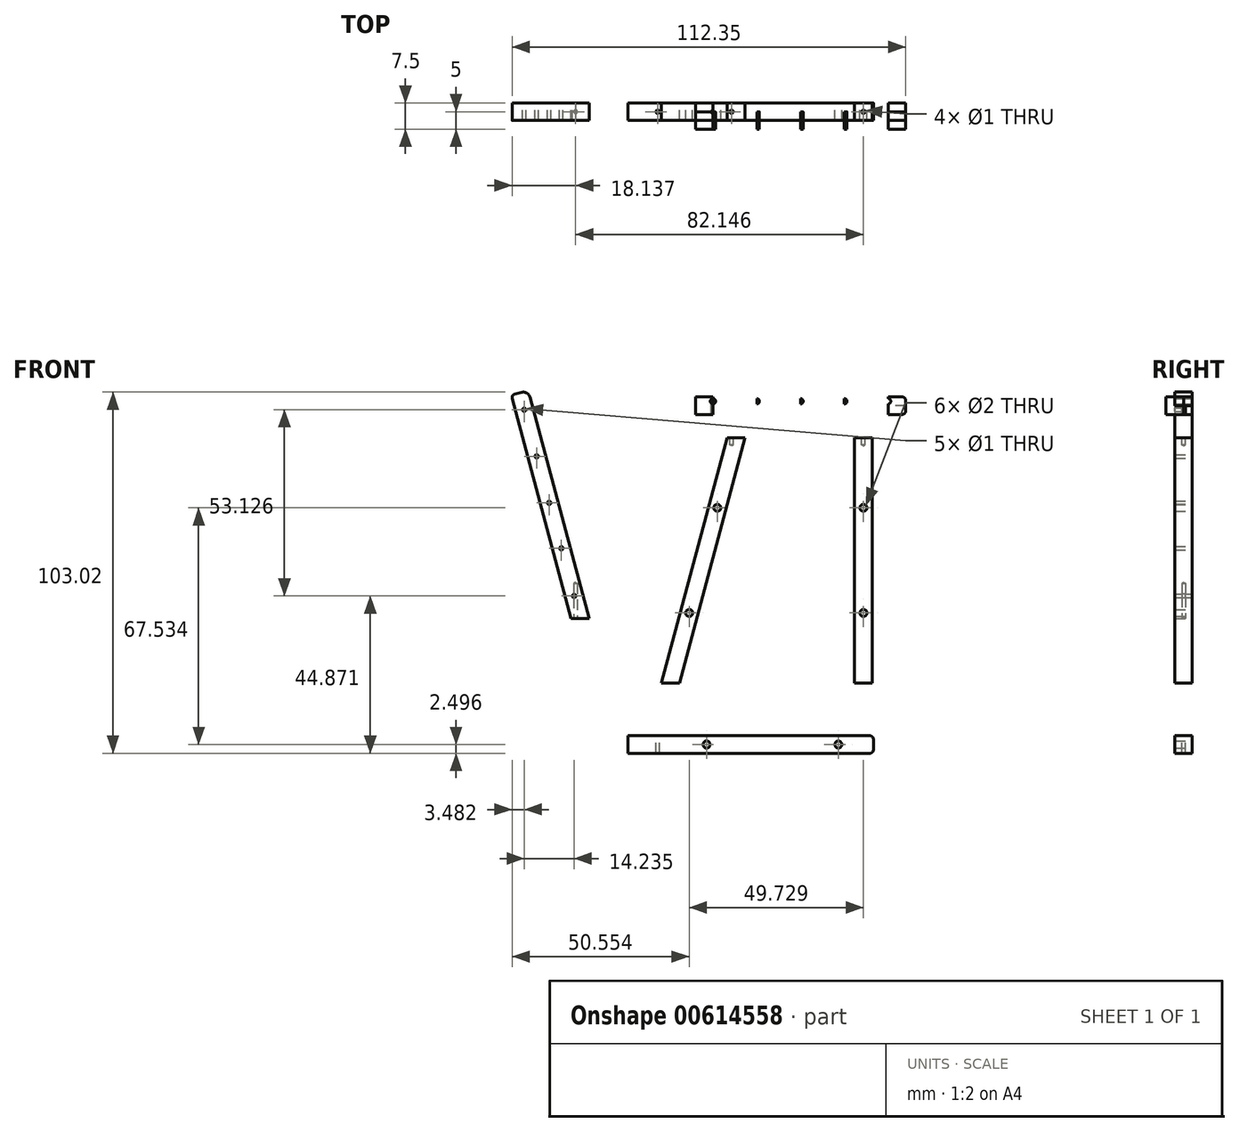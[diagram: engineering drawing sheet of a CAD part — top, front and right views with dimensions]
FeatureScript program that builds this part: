
annotation { "Feature Type Name" : "Feature", "Feature Type Description" : "" }
export const myFeature = defineFeature(function(context is Context, id is Id, definition is map)
    precondition{}
    {
        {
            var Q0;
            Q0=qCreatedBy(makeId("Front.planeOp"),FACE);
            var sketch = newSketch(context, id + "F0", { "sketchPlane" : qUnion([Q0])});
            skLineSegment(sketch, "E0.bottom", {"start": v(19.01, 34.3) * mm, "end": v(24.01, 34.3) * mm});
            skLineSegment(sketch, "E0.top", {"start": v(19.01, -35.7) * mm, "end": v(24.01, -35.7) * mm});
            skLineSegment(sketch, "E0.left", {"start": v(19.01, 34.3) * mm, "end": v(19.01, -35.7) * mm});
            skLineSegment(sketch, "E0.right", {"start": v(24.01, 34.3) * mm, "end": v(24.01, -35.7) * mm});
            skCircle(sketch, "E1", {"center": v(21.51, -15.7) * mm, "radius": 1 * mm});
            skCircle(sketch, "E2", {"center": v(21.51, 14.3) * mm, "radius": 1 * mm});
            skLineSegment(sketch, "E3.bottom", {"start": v(-17.4, 34.3) * mm, "end": v(-12.58, 33.02) * mm});
            skLineSegment(sketch, "E3.top", {"start": v(-35.82, -34.4) * mm, "end": v(-30.99, -35.7) * mm});
            skLineSegment(sketch, "E3.left", {"start": v(-17.4, 34.3) * mm, "end": v(-35.82, -34.4) * mm});
            skLineSegment(sketch, "E3.right", {"start": v(-12.58, 33.02) * mm, "end": v(-30.99, -35.7) * mm});
            skLineSegment(sketch, "E4", {"start": v(19.01, -35.7) * mm, "end": v(-30.99, -35.7) * mm});
            skLineSegment(sketch, "E5", {"start": v(-30.99, -35.7) * mm, "end": v(-36.16, -35.7) * mm});
            skLineSegment(sketch, "E6", {"start": v(-35.82, -34.4) * mm, "end": v(-36.16, -35.7) * mm});
            skLineSegment(sketch, "E7", {"start": v(-17.4, 34.3) * mm, "end": v(-12.23, 34.3) * mm});
            skLineSegment(sketch, "E8", {"start": v(-12.58, 33.02) * mm, "end": v(-12.23, 34.3) * mm});
            skCircle(sketch, "E9", {"center": v(-20.18, 14.3) * mm, "radius": 1 * mm});
            skCircle(sketch, "E10", {"center": v(-28.22, -15.7) * mm, "radius": 1 * mm});
            skLineSegment(sketch, "E11", {"start": v(21.51, 34.3) * mm, "end": v(21.51, 14.3) * mm});
            skLineSegment(sketch, "E12", {"start": v(21.51, -35.7) * mm, "end": v(21.51, -15.7) * mm});
            skLineSegment(sketch, "E13", {"start": v(-17.4, 34.3) * mm, "end": v(-14.82, 34.3) * mm});
            skLineSegment(sketch, "E14", {"start": v(-17.4, 34.3) * mm, "end": v(-16.11, 34.3) * mm});
            skSolve(sketch);
        }
        {
            var Q0;
            Q0=qCreatedBy(makeId("Front.planeOp"),FACE);
            var sketch = newSketch(context, id + "F1", { "sketchPlane" : qUnion([Q0])});
            skLineSegment(sketch, "E15.bottom", {"start": v(-26.42, 45.94) * mm, "end": v(32.58, 45.94) * mm});
            skLineSegment(sketch, "E15.top", {"start": v(-26.42, 40.94) * mm, "end": v(32.58, 40.94) * mm});
            skLineSegment(sketch, "E15.left", {"start": v(-26.42, 45.94) * mm, "end": v(-26.42, 40.94) * mm});
            skLineSegment(sketch, "E15.right", {"start": v(33.58, 44.94) * mm, "end": v(33.58, 41.94) * mm});
            skLineSegment(sketch, "E16", {"start": v(33.58, 43.44) * mm, "end": v(26.08, 43.44) * mm});
            skLineSegment(sketch, "E17", {"start": v(26.08, 43.44) * mm, "end": v(-15.61, 43.44) * mm});
            skCircle(sketch, "E18", {"center": v(-15.61, 43.44) * mm, "radius": 0.75 * mm});
            skCircle(sketch, "E19", {"center": v(26.08, 43.44) * mm, "radius": 0.75 * mm});
            skPoint(sketch, "E20.visualSharp", {"position": v(33.58, 45.94) * mm});
            skArc(sketch, "E20.filletArc", {"start": v(33.58, 44.94) * mm, "mid": v(33.29, 45.65) * mm, "end": v(32.58, 45.94) * mm});
            skPoint(sketch, "E21.visualSharp", {"position": v(33.58, 40.94) * mm});
            skArc(sketch, "E21.filletArc", {"start": v(32.58, 40.94) * mm, "mid": v(33.29, 41.23) * mm, "end": v(33.58, 41.94) * mm});
            skLineSegment(sketch, "E22", {"start": v(-26.42, 45.94) * mm, "end": v(-21.42, 45.94) * mm});
            skLineSegment(sketch, "E23", {"start": v(33.58, 45.94) * mm, "end": v(28.58, 45.94) * mm});
            skLineSegment(sketch, "E24", {"start": v(-21.42, 45.94) * mm, "end": v(-8.92, 45.94) * mm});
            skLineSegment(sketch, "E25", {"start": v(-8.92, 45.94) * mm, "end": v(3.58, 45.94) * mm});
            skLineSegment(sketch, "E26", {"start": v(3.58, 45.94) * mm, "end": v(16.08, 45.94) * mm});
            skLineSegment(sketch, "E27", {"start": v(16.08, 45.94) * mm, "end": v(28.58, 45.94) * mm});
            skLineSegment(sketch, "E28", {"start": v(-21.42, 45.94) * mm, "end": v(-21.42, 40.94) * mm});
            skLineSegment(sketch, "E29", {"start": v(-8.92, 45.94) * mm, "end": v(-8.92, 40.94) * mm});
            skLineSegment(sketch, "E30", {"start": v(3.58, 45.94) * mm, "end": v(3.58, 40.94) * mm});
            skLineSegment(sketch, "E31", {"start": v(16.08, 45.94) * mm, "end": v(16.08, 40.94) * mm});
            skLineSegment(sketch, "E32", {"start": v(28.58, 45.94) * mm, "end": v(28.58, 40.94) * mm});
            skLineSegment(sketch, "E33", {"start": v(-15.61, 43.44) * mm, "end": v(-21.42, 43.44) * mm});
            skLineSegment(sketch, "E34", {"start": v(-21.42, 43.44) * mm, "end": v(-21.42, 45.94) * mm});
            skLineSegment(sketch, "E35", {"start": v(-8.92, 45.94) * mm, "end": v(-8.92, 43.44) * mm});
            skLineSegment(sketch, "E36", {"start": v(-8.92, 45.94) * mm, "end": v(-8.92, 44.7) * mm});
            skLineSegment(sketch, "E37", {"start": v(3.58, 45.94) * mm, "end": v(3.58, 43.44) * mm});
            skLineSegment(sketch, "E38", {"start": v(3.58, 43.44) * mm, "end": v(3.58, 44.7) * mm});
            skLineSegment(sketch, "E39", {"start": v(16.08, 43.44) * mm, "end": v(16.08, 45.94) * mm});
            skLineSegment(sketch, "E40", {"start": v(28.58, 45.94) * mm, "end": v(28.58, 43.44) * mm});
            skLineSegment(sketch, "E41", {"start": v(28.58, 43.44) * mm, "end": v(28.58, 44.7) * mm});
            skLineSegment(sketch, "E42", {"start": v(-21.42, 45.94) * mm, "end": v(-21.42, 44.7) * mm});
            skCircle(sketch, "E43", {"center": v(-21.42, 44.7) * mm, "radius": 0.75 * mm});
            skCircle(sketch, "E44", {"center": v(-8.92, 44.7) * mm, "radius": 0.75 * mm});
            skCircle(sketch, "E45", {"center": v(3.58, 44.7) * mm, "radius": 0.75 * mm});
            skCircle(sketch, "E46", {"center": v(16.08, 44.7) * mm, "radius": 0.75 * mm});
            skCircle(sketch, "E47", {"center": v(28.58, 44.7) * mm, "radius": 0.75 * mm});
            skSolve(sketch);
        }
        {
            var Q0;
            {var subQ1=sQuery(id+"F1.wireOp",EDGE,"E15.bottom");Q0=makeQuery(id+"F1.imprint","IMPRINT",FACE,{"disambiguationData":[TD([[makeQuery(id+"F1.imprint","IMPRINT",EDGE,{"derivedFrom":subQ1}),-1.0]])]});}
            var Q1;
            {var subQ3=sQuery(id+"F0.wireOp",EDGE,"E0.left");Q1=makeQuery(id+"F0.imprint","IMPRINT",FACE,{"disambiguationData":[TD([[makeQuery(id+"F0.imprint","IMPRINT",EDGE,{"derivedFrom":subQ3}),1.0]])]});}
            var Q2;
            Q2=makeQuery(id+"F0.imprint","IMPRINT",FACE,{"disambiguationData":[TD([[makeQuery(id+"F0.imprint","IMPRINT",EDGE,{"derivedFrom":sQuery(id+"F0.wireOp",EDGE,"E3.bottom")}),-1.0]])]});
            var Q3;
            Q3=makeQuery(id+"F0.imprint","IMPRINT",FACE,{"disambiguationData":[TD([[makeQuery(id+"F0.imprint","IMPRINT",EDGE,{"derivedFrom":sQuery(id+"F0.wireOp",EDGE,"E3.bottom")}),1.0]])]});
            var Q4;
            Q4=makeQuery(id+"F0.imprint","IMPRINT",FACE,{"disambiguationData":[TD([[makeQuery(id+"F0.imprint","IMPRINT",EDGE,{"derivedFrom":sQuery(id+"F0.wireOp",EDGE,"E3.top")}),-1.0]])]});
            extrude(context, id + "F2", {"entities" : qUnion([Q0, Q1, Q2, Q3, Q4]), "endBound" : BoundingType.SYMMETRIC, "depth" : 5 * mm, "offsetDistance" : 25 * mm});
        }
        {
            var Q0;
            Q0=qCreatedBy(makeId("Front.planeOp"),FACE);
            var sketch = newSketch(context, id + "F3", { "sketchPlane" : qUnion([Q0])});
            skLineSegment(sketch, "E48.bottom", {"start": v(-45.64, -50.72) * mm, "end": v(23.36, -50.72) * mm});
            skLineSegment(sketch, "E48.top", {"start": v(-45.64, -55.72) * mm, "end": v(23.36, -55.72) * mm});
            skLineSegment(sketch, "E48.left", {"start": v(-45.64, -50.72) * mm, "end": v(-45.64, -55.72) * mm});
            skLineSegment(sketch, "E48.right", {"start": v(24.36, -51.72) * mm, "end": v(24.36, -54.72) * mm});
            skLineSegment(sketch, "E49", {"start": v(24.36, -53.22) * mm, "end": v(14.36, -53.22) * mm});
            skLineSegment(sketch, "E50", {"start": v(14.36, -53.22) * mm, "end": v(-23.26, -53.22) * mm});
            skCircle(sketch, "E51", {"center": v(-23.26, -53.22) * mm, "radius": 1 * mm});
            skCircle(sketch, "E52", {"center": v(14.36, -53.22) * mm, "radius": 1 * mm});
            skPoint(sketch, "E53.visualSharp", {"position": v(24.36, -50.72) * mm});
            skArc(sketch, "E53.filletArc", {"start": v(24.36, -51.72) * mm, "mid": v(24.07, -51.02) * mm, "end": v(23.36, -50.72) * mm});
            skPoint(sketch, "E54.visualSharp", {"position": v(24.36, -55.72) * mm});
            skArc(sketch, "E54.filletArc", {"start": v(23.36, -55.72) * mm, "mid": v(24.07, -55.43) * mm, "end": v(24.36, -54.72) * mm});
            skSolve(sketch);
        }
        {
            var Q0;
            Q0=makeQuery(id+"F3.imprint","IMPRINT",FACE,{"disambiguationData":[TD([[makeQuery(id+"F3.imprint","IMPRINT",EDGE,{"derivedFrom":sQuery(id+"F3.wireOp",EDGE,"E48.bottom")}),-1.0]])]});
            extrude(context, id + "F4", {"entities" : qUnion([Q0]), "endBound" : BoundingType.SYMMETRIC, "depth" : 5 * mm, "offsetDistance" : 25 * mm});
        }
        {
            var Q0;
            Q0=makeQuery(id+"F2.opExtrude","SWEPT_FACE",FACE,{"disambiguationData":[OSD([sQuery(id+"F0.wireOp",EDGE,"E7"),sQuery(id+"F0.wireOp",EDGE,"E13"),sQuery(id+"F0.wireOp",EDGE,"E14")])]});
            var sketch = newSketch(context, id + "F5", { "sketchPlane" : qUnion([Q0])});
            skLineSegment(sketch, "E55", {"start": v(-17.4, 0) * mm, "end": v(-12.23, 0) * mm});
            skLineSegment(sketch, "E56", {"start": v(-17.4, 0) * mm, "end": v(-14.82, 0) * mm});
            skLineSegment(sketch, "E57", {"start": v(-14.82, 0) * mm, "end": v(-16.11, 0) * mm});
            skSolve(sketch);
        }
        {
            var Q0;
            Q0=sQuery(id+"F5.wireOp",VERTEX,"E57.end");
            var Q1;
            Q1=makeQuery(id+"F2.opExtrude","SWEPT_BODY",BODY,{"disambiguationData":[OSD([sQuery(id+"F0.wireOp",EDGE,"E3.left"),sQuery(id+"F0.wireOp",EDGE,"E3.right"),sQuery(id+"F0.wireOp",EDGE,"E5"),sQuery(id+"F0.wireOp",EDGE,"E6"),sQuery(id+"F0.wireOp",EDGE,"E7"),sQuery(id+"F0.wireOp",EDGE,"E8"),sQuery(id+"F0.wireOp",EDGE,"E9"),sQuery(id+"F0.wireOp",EDGE,"E10"),sQuery(id+"F0.wireOp",EDGE,"E13"),sQuery(id+"F0.wireOp",EDGE,"E14")])]});
            hole(context, id + "F6", {"style" : HoleStyle.SIMPLE, "endStyle" : HoleEndStyle.BLIND, "holeDiameter" : 1 * mm, "majorDiameter" : 5 * mm, "holeDepth" : 2 * mm, "isTappedThrough" : true, "tappedDepth" : 12 * mm, "tapClearance" : 3, "locations" : qUnion([Q0]), "scope" : qUnion([Q1])});
        }
        {
            var Q0;
            Q0=makeQuery(id+"F2.opExtrude","SWEPT_FACE",FACE,{"disambiguationData":[OSD([sQuery(id+"F0.wireOp",EDGE,"E0.bottom")])]});
            var sketch = newSketch(context, id + "F7", { "sketchPlane" : qUnion([Q0])});
            skLineSegment(sketch, "E58", {"start": v(19.01, 0) * mm, "end": v(24.01, 0) * mm});
            skLineSegment(sketch, "E59", {"start": v(19.01, 0) * mm, "end": v(21.51, 0) * mm});
            skSolve(sketch);
        }
        {
            var Q0;
            Q0=sQuery(id+"F7.wireOp",VERTEX,"E59.end");
            var Q1;
            Q1=makeQuery(id+"F2.opExtrude","SWEPT_BODY",BODY,{"disambiguationData":[OSD([sQuery(id+"F0.wireOp",EDGE,"E0.bottom"),sQuery(id+"F0.wireOp",EDGE,"E0.top"),sQuery(id+"F0.wireOp",EDGE,"E0.left"),sQuery(id+"F0.wireOp",EDGE,"E0.right"),sQuery(id+"F0.wireOp",EDGE,"E1"),sQuery(id+"F0.wireOp",EDGE,"E2")])]});
            hole(context, id + "F8", {"style" : HoleStyle.SIMPLE, "endStyle" : HoleEndStyle.BLIND, "holeDiameter" : 1 * mm, "majorDiameter" : 5 * mm, "holeDepth" : 2 * mm, "isTappedThrough" : true, "tappedDepth" : 12 * mm, "tapClearance" : 3, "locations" : qUnion([Q0]), "scope" : qUnion([Q1])});
        }
        {
            var Q0;
            Q0=qCreatedBy(makeId("Front.planeOp"),FACE);
            var sketch = newSketch(context, id + "F9", { "sketchPlane" : qUnion([Q0])});
            skLineSegment(sketch, "E60.bottom", {"start": v(-79, 46.46) * mm, "end": v(-74.17, 47.75) * mm});
            skLineSegment(sketch, "E60.top", {"start": v(-61.93, -17.25) * mm, "end": v(-57.1, -15.95) * mm});
            skLineSegment(sketch, "E60.left", {"start": v(-79, 46.46) * mm, "end": v(-61.93, -17.25) * mm});
            skLineSegment(sketch, "E60.right", {"start": v(-74.17, 47.75) * mm, "end": v(-57.1, -15.95) * mm});
            skLineSegment(sketch, "E61", {"start": v(-61.93, -17.25) * mm, "end": v(-56.75, -17.25) * mm});
            skLineSegment(sketch, "E62", {"start": v(-57.1, -15.95) * mm, "end": v(-56.75, -17.25) * mm});
            skLineSegment(sketch, "E63", {"start": v(-59.34, -17.25) * mm, "end": v(-64.7, 2.75) * mm});
            skCircle(sketch, "E64", {"center": v(-64.7, 2.75) * mm, "radius": 0.5 * mm});
            skLineSegment(sketch, "E65", {"start": v(-64.7, 2.75) * mm, "end": v(-76.58, 47.1) * mm});
            skLineSegment(sketch, "E66", {"start": v(-76.58, 47.1) * mm, "end": v(-75.29, 42.28) * mm});
            skLineSegment(sketch, "E67", {"start": v(-75.29, 42.28) * mm, "end": v(-71.73, 29) * mm});
            skLineSegment(sketch, "E68", {"start": v(-71.73, 29) * mm, "end": v(-68.17, 15.71) * mm});
            skLineSegment(sketch, "E69", {"start": v(-68.17, 15.71) * mm, "end": v(-64.61, 2.43) * mm});
            skLineSegment(sketch, "E70", {"start": v(-64.61, 2.43) * mm, "end": v(-61.05, -10.85) * mm});
            skCircle(sketch, "E71", {"center": v(-61.05, -10.85) * mm, "radius": 0.5 * mm});
            skCircle(sketch, "E72", {"center": v(-75.29, 42.28) * mm, "radius": 0.5 * mm});
            skCircle(sketch, "E73", {"center": v(-71.73, 29) * mm, "radius": 0.5 * mm});
            skCircle(sketch, "E74", {"center": v(-68.17, 15.71) * mm, "radius": 0.5 * mm});
            skSolve(sketch);
        }
        {
            var Q0;
            Q0=makeQuery(id+"F2.opExtrude","SWEPT_FACE",FACE,{"disambiguationData":[OSD([sQuery(id+"F1.wireOp",EDGE,"E15.bottom")])]});
            var sketch = newSketch(context, id + "F10", { "sketchPlane" : qUnion([Q0])});
            skLineSegment(sketch, "E75", {"start": v(-26.42, 0) * mm, "end": v(-21.42, 0) * mm});
            skPoint(sketch, "E75.endSnap0", {"position": v(-26.42, 0) * mm});
            skSolve(sketch);
        }
        {
            var Q0;
            Q0=makeQuery(id+"F9.imprint","IMPRINT",FACE,{"disambiguationData":[TD([[makeQuery(id+"F9.imprint","IMPRINT",EDGE,{"derivedFrom":sQuery(id+"F9.wireOp",EDGE,"E60.bottom")}),-1.0]])]});
            var Q1;
            {var subQ0=sQuery(id+"F9.wireOp",EDGE,"E62");Q1=makeQuery(id+"F9.imprint","IMPRINT",FACE,{"disambiguationData":[TD([[makeQuery(id+"F9.imprint","IMPRINT",EDGE,{"derivedFrom":subQ0}),-1.0]])]});}
            var Q2;
            {var subQ0=sQuery(id+"F9.wireOp",EDGE,"E61");var subQ3=sQuery(id+"F9.wireOp",EDGE,"E63");var subQ5=makeQuery(id+"F9.imprint","INTERSECT",VERTEX,{"derivedFrom":[subQ0,subQ3]});Q2=makeQuery(id+"F9.imprint","IMPRINT",FACE,{"disambiguationData":[TD([[makeQuery(id+"F9.imprint","IMPRINT",EDGE,{"disambiguationData":[TD([[subQ5,-1.0]])],"derivedFrom":subQ3}),1.0]])]});}
            extrude(context, id + "F11", {"entities" : qUnion([Q0, Q1, Q2]), "endBound" : BoundingType.SYMMETRIC, "depth" : 5 * mm, "offsetDistance" : 25 * mm});
        }
        {
            var Q0;
            Q0=makeQuery(id+"F11.opExtrude","SWEPT_FACE",FACE,{"disambiguationData":[OSD([sQuery(id+"F9.wireOp",EDGE,"E61")])]});
            var sketch = newSketch(context, id + "F12", { "sketchPlane" : qUnion([Q0])});
            skLineSegment(sketch, "E76", {"start": v(-61.93, 0) * mm, "end": v(-56.75, 0) * mm});
            skLineSegment(sketch, "E77", {"start": v(-56.75, 0) * mm, "end": v(-59.34, 0) * mm});
            skLineSegment(sketch, "E78", {"start": v(-59.34, 0) * mm, "end": v(-61.93, 0) * mm});
            skLineSegment(sketch, "E79", {"start": v(-61.93, 0) * mm, "end": v(-60.63, 0) * mm});
            skSolve(sketch);
        }
        {
            var Q0;
            Q0=sQuery(id+"F12.wireOp",VERTEX,"E79.end");
            var Q1;
            Q1=makeQuery(id+"F11.opExtrude","SWEPT_BODY",BODY,{"disambiguationData":[OSD([sQuery(id+"F9.wireOp",EDGE,"E60.bottom"),sQuery(id+"F9.wireOp",EDGE,"E60.left"),sQuery(id+"F9.wireOp",EDGE,"E60.right"),sQuery(id+"F9.wireOp",EDGE,"E61"),sQuery(id+"F9.wireOp",EDGE,"E62"),sQuery(id+"F9.wireOp",EDGE,"E64")])]});
            hole(context, id + "F13", {"style" : HoleStyle.SIMPLE, "endStyle" : HoleEndStyle.BLIND, "holeDiameter" : 1 * mm, "majorDiameter" : 5 * mm, "holeDepth" : 10 * mm, "isTappedThrough" : true, "tappedDepth" : 12 * mm, "tapClearance" : 3, "locations" : qUnion([Q0]), "scope" : qUnion([Q1])});
        }
        {
            var Q0;
            Q0=sQuery(id+"F10.wireOp",VERTEX,"E75.end");
            var Q1;
            Q1=makeQuery(id+"F2.opExtrude","SWEPT_BODY",BODY,{"disambiguationData":[OSD([sQuery(id+"F1.wireOp",EDGE,"E15.bottom"),sQuery(id+"F1.wireOp",EDGE,"E15.top"),sQuery(id+"F1.wireOp",EDGE,"E15.left"),sQuery(id+"F1.wireOp",EDGE,"E15.right"),sQuery(id+"F1.wireOp",EDGE,"E18"),sQuery(id+"F1.wireOp",EDGE,"E19"),sQuery(id+"F1.wireOp",EDGE,"E20.filletArc"),sQuery(id+"F1.wireOp",EDGE,"E21.filletArc")])]});
            hole(context, id + "F14", {"style" : HoleStyle.SIMPLE, "endStyle" : HoleEndStyle.BLIND, "holeDiameter" : 1 * mm, "majorDiameter" : 5 * mm, "holeDepth" : 10 * mm, "isTappedThrough" : true, "tappedDepth" : 12 * mm, "tapClearance" : 3, "locations" : qUnion([Q0]), "scope" : qUnion([Q1])});
        }
        {
            var Q0;
            Q0=makeQuery(id+"F4.opExtrude","SWEPT_FACE",FACE,{"disambiguationData":[OSD([sQuery(id+"F3.wireOp",EDGE,"E48.bottom")])]});
            var sketch = newSketch(context, id + "F15", { "sketchPlane" : qUnion([Q0])});
            skPoint(sketch, "E80.endSnap0", {"position": v(-45.64, 0) * mm});
            skLineSegment(sketch, "E81", {"start": v(-45.64, 0) * mm, "end": v(-37.2, 0) * mm});
            skSolve(sketch);
        }
        {
            var Q0;
            Q0=sQuery(id+"F15.wireOp",VERTEX,"E81.end");
            var Q1;
            Q1=makeQuery(id+"F4.opExtrude","SWEPT_BODY",BODY,{"disambiguationData":[OSD([sQuery(id+"F3.wireOp",EDGE,"E48.bottom"),sQuery(id+"F3.wireOp",EDGE,"E48.top"),sQuery(id+"F3.wireOp",EDGE,"E48.left"),sQuery(id+"F3.wireOp",EDGE,"E48.right"),sQuery(id+"F3.wireOp",EDGE,"E51"),sQuery(id+"F3.wireOp",EDGE,"E52"),sQuery(id+"F3.wireOp",EDGE,"E53.filletArc"),sQuery(id+"F3.wireOp",EDGE,"E54.filletArc")])]});
            hole(context, id + "F16", {"style" : HoleStyle.SIMPLE, "endStyle" : HoleEndStyle.BLIND, "holeDiameter" : 1 * mm, "majorDiameter" : 5 * mm, "holeDepth" : 10 * mm, "isTappedThrough" : true, "tappedDepth" : 12 * mm, "tapClearance" : 3, "locations" : qUnion([Q0]), "scope" : qUnion([Q1])});
        }
        {
            var Q0;
            Q0=makeQuery(id+"F11.opExtrude","SWEPT_EDGE",EDGE,{"disambiguationData":[OSD([sQuery(id+"F9.wireOp",EDGE,"E60.bottom"),sQuery(id+"F9.wireOp",EDGE,"E60.left")])]});
            fillet(context, id + "F17", {"entities" : qUnion([Q0]), "radius" : 1 * mm, "tangentPropagation" : true, "allowEdgeOverflow" : false});
        }
        {
            var Q0;
            Q0=makeQuery(id+"F11.opExtrude","SWEPT_EDGE",EDGE,{"disambiguationData":[OSD([sQuery(id+"F9.wireOp",EDGE,"E60.bottom"),sQuery(id+"F9.wireOp",EDGE,"E60.right")])]});
            fillet(context, id + "F18", {"entities" : qUnion([Q0]), "radius" : 2 * mm, "tangentPropagation" : true, "allowEdgeOverflow" : false});
        }
        {
            var Q0;
            {var subQ1=sQuery(id+"F1.wireOp",EDGE,"E15.left");Q0=makeQuery(id+"F1.imprint","IMPRINT",FACE,{"disambiguationData":[TD([[makeQuery(id+"F1.imprint","IMPRINT",EDGE,{"derivedFrom":subQ1}),1.0]])]});}
            var Q1;
            {var subQ0=sQuery(id+"F1.wireOp",EDGE,"E28");Q1=makeQuery(id+"F1.imprint","IMPRINT",FACE,{"disambiguationData":[TD([[makeQuery(id+"F1.imprint","IMPRINT",EDGE,{"derivedFrom":subQ0}),1.0]])]});}
            var Q2;
            {var subQ13=sQuery(id+"F1.wireOp",EDGE,"E24");Q2=makeQuery(id+"F1.imprint","IMPRINT",FACE,{"disambiguationData":[TD([[makeQuery(id+"F1.imprint","IMPRINT",EDGE,{"derivedFrom":subQ13}),-1.0]])]});}
            var Q3;
            {var subQ0=sQuery(id+"F1.wireOp",EDGE,"E29");Q3=makeQuery(id+"F1.imprint","IMPRINT",FACE,{"disambiguationData":[TD([[makeQuery(id+"F1.imprint","IMPRINT",EDGE,{"derivedFrom":subQ0}),1.0]])]});}
            var Q4;
            {var subQ1=sQuery(id+"F1.wireOp",EDGE,"E25");Q4=makeQuery(id+"F1.imprint","IMPRINT",FACE,{"disambiguationData":[TD([[makeQuery(id+"F1.imprint","IMPRINT",EDGE,{"derivedFrom":subQ1}),-1.0]])]});}
            var Q5;
            {var subQ0=sQuery(id+"F1.wireOp",EDGE,"E30");Q5=makeQuery(id+"F1.imprint","IMPRINT",FACE,{"disambiguationData":[TD([[makeQuery(id+"F1.imprint","IMPRINT",EDGE,{"derivedFrom":subQ0}),1.0]])]});}
            var Q6;
            {var subQ6=sQuery(id+"F1.wireOp",EDGE,"E26");Q6=makeQuery(id+"F1.imprint","IMPRINT",FACE,{"disambiguationData":[TD([[makeQuery(id+"F1.imprint","IMPRINT",EDGE,{"derivedFrom":subQ6}),-1.0]])]});}
            var Q7;
            {var subQ6=sQuery(id+"F1.wireOp",EDGE,"E31");Q7=makeQuery(id+"F1.imprint","IMPRINT",FACE,{"disambiguationData":[TD([[makeQuery(id+"F1.imprint","IMPRINT",EDGE,{"derivedFrom":subQ6}),1.0]])]});}
            var Q8;
            {var subQ0=sQuery(id+"F1.wireOp",EDGE,"E27");Q8=makeQuery(id+"F1.imprint","IMPRINT",FACE,{"disambiguationData":[TD([[makeQuery(id+"F1.imprint","IMPRINT",EDGE,{"derivedFrom":subQ0}),-1.0]])]});}
            var Q9;
            {var subQ1=sQuery(id+"F1.wireOp",EDGE,"E20.filletArc");Q9=makeQuery(id+"F1.imprint","IMPRINT",FACE,{"disambiguationData":[TD([[makeQuery(id+"F1.imprint","IMPRINT",EDGE,{"derivedFrom":subQ1}),1.0]])]});}
            var Q10;
            {var subQ4=sQuery(id+"F1.wireOp",EDGE,"E21.filletArc");Q10=makeQuery(id+"F1.imprint","IMPRINT",FACE,{"disambiguationData":[TD([[makeQuery(id+"F1.imprint","IMPRINT",EDGE,{"derivedFrom":subQ4}),1.0]])]});}
            extrude(context, id + "F19", {"entities" : qUnion([Q0, Q1, Q2, Q3, Q4, Q5, Q6, Q7, Q8, Q9, Q10]), "depth" : 5 * mm, "offsetDistance" : 25 * mm});
        }
    });
